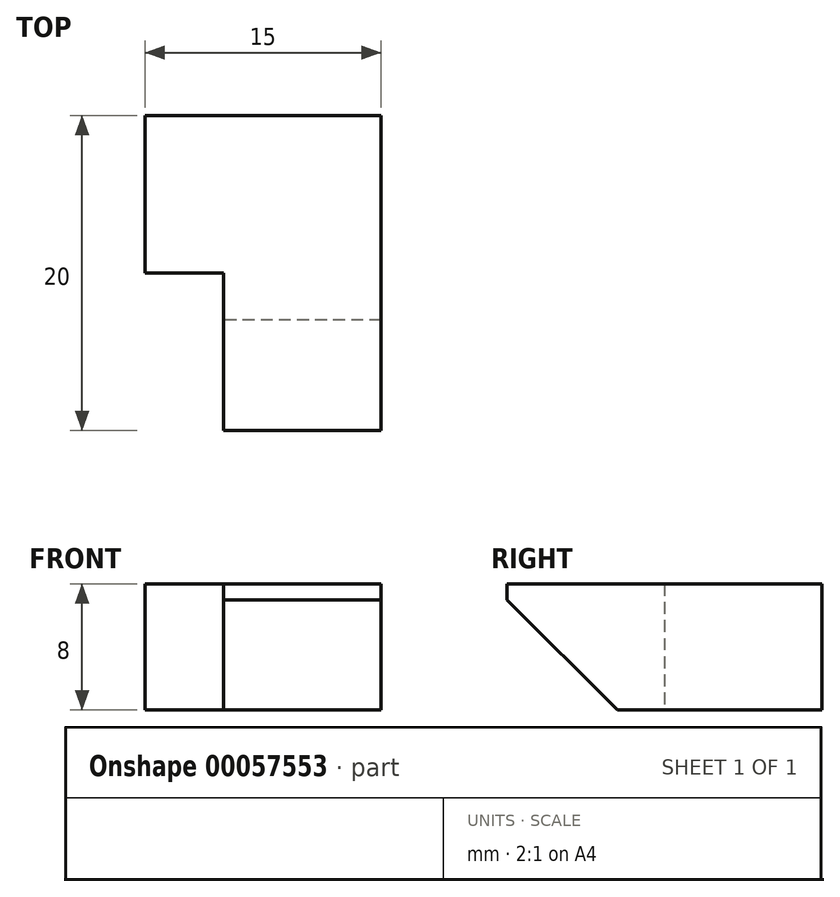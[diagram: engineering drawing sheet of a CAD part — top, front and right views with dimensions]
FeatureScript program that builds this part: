
annotation { "Feature Type Name" : "Feature", "Feature Type Description" : "" }
export const myFeature = defineFeature(function(context is Context, id is Id, definition is map)
    precondition{}
    {
        {
            var Q0;
            Q0=qCreatedBy(makeId("Top.planeOp"),FACE);
            var sketch = newSketch(context, id + "F0", { "sketchPlane" : qUnion([Q0])});
            skLineSegment(sketch, "E0.rect.bottom", {"start": v(10, 10) * mm, "end": v(-10, 10) * mm});
            skLineSegment(sketch, "E0.rect.top", {"start": v(10, -10) * mm, "end": v(-10, -10) * mm});
            skLineSegment(sketch, "E0.rect.left", {"start": v(10, 10) * mm, "end": v(10, -10) * mm});
            skLineSegment(sketch, "E0.rect.right", {"start": v(-10, 10) * mm, "end": v(-10, -10) * mm});
            skPoint(sketch, "E0.rect.middle", {"position": v(0, 0) * mm});
            skLineSegment(sketch, "E1", {"start": v(0, -10) * mm, "end": v(0, 0) * mm});
            skLineSegment(sketch, "E2", {"start": v(0, 0) * mm, "end": v(-10, 0) * mm});
            skLineSegment(sketch, "E3", {"start": v(-5, 0) * mm, "end": v(-5, 10) * mm});
            skSolve(sketch);
        }
        {
            var Q0;
            {var subQ1=sQuery(id+"F0.wireOp",EDGE,"E0.rect.left");Q0=makeQuery(id+"F0.imprint","IMPRINT",FACE,{"disambiguationData":[TD([[makeQuery(id+"F0.imprint","IMPRINT",EDGE,{"derivedFrom":subQ1}),-1.0]])]});}
            extrude(context, id + "F1", {"entities" : qUnion([Q0]), "depth" : 8 * mm});
        }
        {
            var Q0;
            Q0=makeQuery(id+"F1.opExtrude","CAP_EDGE",EDGE,{"disambiguationData":[OSD([sQuery(id+"F0.wireOp",EDGE,"E0.rect.top")])],"isStart":true});
            chamfer(context, id + "F2", {"entities" : qUnion([Q0]), "width" : 7 * mm, "tangentPropagation" : true});
        }
    });
